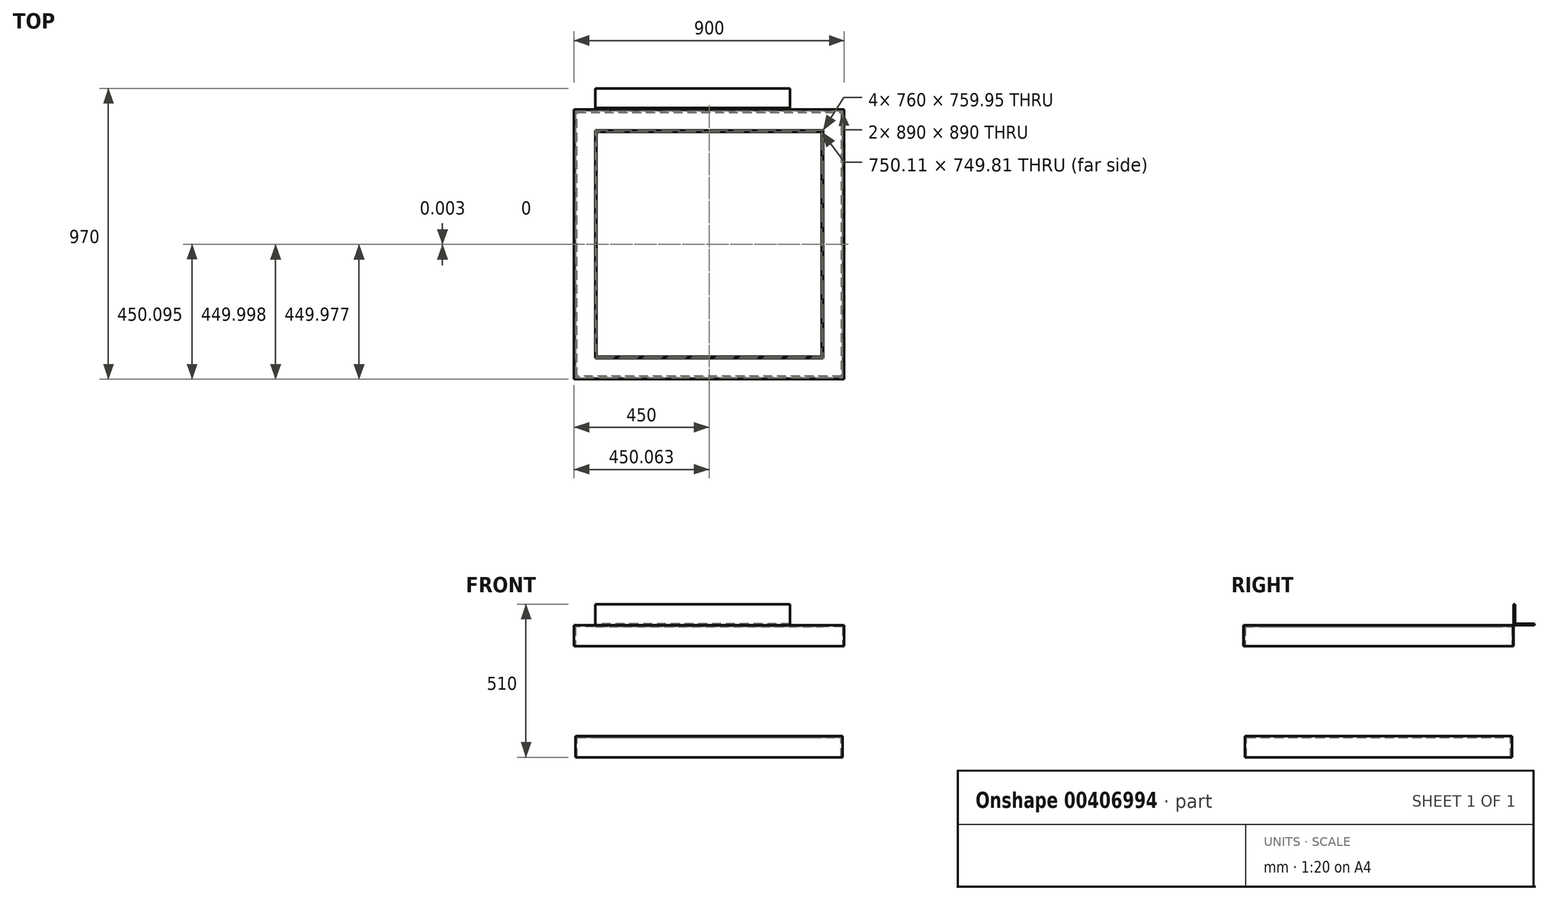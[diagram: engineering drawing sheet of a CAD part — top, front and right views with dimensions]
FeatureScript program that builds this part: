
annotation { "Feature Type Name" : "Feature", "Feature Type Description" : "" }
export const myFeature = defineFeature(function(context is Context, id is Id, definition is map)
    precondition{}
    {
        {
            var Q0;
            Q0=qCreatedBy(makeId("Top.planeOp"),FACE);
            var sketch = newSketch(context, id + "F0", { "sketchPlane" : qUnion([Q0])});
            skLineSegment(sketch, "E0", {"start": v(0, 0) * mm, "end": v(0, -900) * mm});
            skLineSegment(sketch, "E1", {"start": v(0, 0) * mm, "end": v(900, 0) * mm});
            skLineSegment(sketch, "E2", {"start": v(900, 0) * mm, "end": v(900, -899.42) * mm});
            skLineSegment(sketch, "E3", {"start": v(900, -899.42) * mm, "end": v(0, -900) * mm});
            skSolve(sketch);
        }
        {
            var Q0;
            Q0=qCreatedBy(makeId("Front.planeOp"),FACE);
            cPlane(context, id + "F1", {"entities" : qUnion([Q0]), "cplaneType" : CPlaneType.OFFSET, "offset" : 450 * mm, "width" : 150 * mm, "height" : 150 * mm});
        }
        {
            var Q0;
            Q0=qCreatedBy(id+"F1.planeOp",FACE);
            var sketch = newSketch(context, id + "F2", { "sketchPlane" : qUnion([Q0])});
            skLineSegment(sketch, "E4", {"start": v(0, 0) * mm, "end": v(70, 0) * mm});
            skLineSegment(sketch, "E5", {"start": v(70, 0) * mm, "end": v(70, -5) * mm});
            skLineSegment(sketch, "E6", {"start": v(0, -70) * mm, "end": v(0, 0) * mm});
            skLineSegment(sketch, "E7", {"start": v(70, -5) * mm, "end": v(5, -5) * mm});
            skLineSegment(sketch, "E8", {"start": v(5, -5) * mm, "end": v(5, -70) * mm});
            skLineSegment(sketch, "E9", {"start": v(5, -70) * mm, "end": v(0, -70) * mm});
            skSolve(sketch);
        }
        {
            var Q0;
            Q0 = qSketchRegion(id + "F2", true);
            var Q1;
            Q1 = qConstructionFilter(qBodyType(qCreatedBy(id + "F0" ,EDGE), BodyType.WIRE), ConstructionObject.NO);
            sweep(context, id + "F3", {"profiles" : qUnion([Q0]), "path" : qUnion([Q1])});
        }
        {
            var Q0;
            Q0=makeQuery(id+"F3.opSweep","SWEPT_FACE",FACE,{"disambiguationData":[OSD([sQuery(id+"F0.wireOp",EDGE,"E0"),sQuery(id+"F2.wireOp",EDGE,"E9")])]});
            var sketch = newSketch(context, id + "F4", { "sketchPlane" : qUnion([Q0])});
            skLineSegment(sketch, "E10", {"start": v(0, 0) * mm, "end": v(0, 70) * mm});
            skLineSegment(sketch, "E11", {"start": v(0, 70) * mm, "end": v(5, 70) * mm});
            skLineSegment(sketch, "E12", {"start": v(5, 70) * mm, "end": v(5, 5) * mm});
            skLineSegment(sketch, "E13", {"start": v(5, 5) * mm, "end": v(70, 5) * mm});
            skLineSegment(sketch, "E14", {"start": v(70, 5) * mm, "end": v(70, 0) * mm});
            skLineSegment(sketch, "E15", {"start": v(70, 0) * mm, "end": v(0, 0) * mm});
            skSolve(sketch);
        }
        {
            var Q0;
            Q0 = qSketchRegion(id + "F4", true);
            extrude(context, id + "F5", {"entities" : qUnion([Q0]), "operationType" : NewBodyOperationType.ADD, "depth" : 650 * mm});
        }
        {
            var Q0;
            Q0=makeQuery(id+"F3.opSweep","SWEPT_BODY",BODY,{"disambiguationData":[OSD([sQuery(id+"F0.wireOp",EDGE,"E1"),sQuery(id+"F2.wireOp",EDGE,"E4"),sQuery(id+"F2.wireOp",EDGE,"E5"),sQuery(id+"F2.wireOp",EDGE,"E6"),sQuery(id+"F2.wireOp",EDGE,"E7"),sQuery(id+"F2.wireOp",EDGE,"E8"),sQuery(id+"F2.wireOp",EDGE,"E9")])]});
            var Q1;
            Q1=qCreatedBy(id+"F1.planeOp",FACE);
            mirror(context, id + "F6", {"entities" : qUnion([Q0]), "mirrorPlane" : qUnion([Q1])});
        }
        {
            var Q0;
            Q0=qCreatedBy(makeId("Right.planeOp"),FACE);
            cPlane(context, id + "F7", {"entities" : qUnion([Q0]), "cplaneType" : CPlaneType.OFFSET, "offset" : 450 * mm, "width" : 150 * mm, "height" : 150 * mm});
        }
        {
            var Q0;
            Q0=makeQuery(id+"F6.opPattern","COPY",BODY,{"derivedFrom":makeQuery(id+"F3.opSweep","SWEPT_BODY",BODY,{"disambiguationData":[OSD([sQuery(id+"F0.wireOp",EDGE,"E1"),sQuery(id+"F2.wireOp",EDGE,"E4"),sQuery(id+"F2.wireOp",EDGE,"E5"),sQuery(id+"F2.wireOp",EDGE,"E6"),sQuery(id+"F2.wireOp",EDGE,"E7"),sQuery(id+"F2.wireOp",EDGE,"E8"),sQuery(id+"F2.wireOp",EDGE,"E9")])]}),"instanceName":"1"});
            var Q1;
            Q1=makeQuery(id+"F3.opSweep","SWEPT_BODY",BODY,{"disambiguationData":[OSD([sQuery(id+"F0.wireOp",EDGE,"E1"),sQuery(id+"F2.wireOp",EDGE,"E4"),sQuery(id+"F2.wireOp",EDGE,"E5"),sQuery(id+"F2.wireOp",EDGE,"E6"),sQuery(id+"F2.wireOp",EDGE,"E7"),sQuery(id+"F2.wireOp",EDGE,"E8"),sQuery(id+"F2.wireOp",EDGE,"E9")])]});
            var Q2;
            Q2=qCreatedBy(id+"F7.planeOp",FACE);
            mirror(context, id + "F8", {"entities" : qUnion([Q0, Q1]), "mirrorPlane" : qUnion([Q2])});
        }
        {
            var Q0;
            Q0=qCreatedBy(id+"F7.planeOp",FACE);
            var sketch = newSketch(context, id + "F9", { "sketchPlane" : qUnion([Q0])});
            skLineSegment(sketch, "E16", {"start": v(-70, -128.07) * mm, "end": v(-70, -133.07) * mm});
            skLineSegment(sketch, "E17", {"start": v(-5, -370) * mm, "end": v(-5, -440) * mm});
            skLineSegment(sketch, "E18", {"start": v(-5, -370) * mm, "end": v(-75, -370) * mm});
            skLineSegment(sketch, "E19", {"start": v(-75, -370) * mm, "end": v(-75, -375) * mm});
            skLineSegment(sketch, "E20", {"start": v(-75, -375) * mm, "end": v(-10, -375) * mm});
            skLineSegment(sketch, "E21", {"start": v(-10, -375) * mm, "end": v(-10, -440) * mm});
            skLineSegment(sketch, "E22", {"start": v(-10, -440) * mm, "end": v(-5, -440) * mm});
            skSolve(sketch);
        }
        {
            var Q0;
            Q0=qCreatedBy(makeId("Top.planeOp"),FACE);
            var Q1;
            Q1=sQuery(id+"F9.wireOp",VERTEX,"E18.start");
            cPlane(context, id + "F10", {"entities" : qUnion([Q0, Q1]), "cplaneType" : CPlaneType.PLANE_POINT, "offset" : 25 * mm, "oppositeDirection" : true, "width" : 150 * mm, "height" : 150 * mm});
        }
        {
            var Q0;
            Q0=qCreatedBy(id+"F10.planeOp",FACE);
            var sketch = newSketch(context, id + "F11", { "sketchPlane" : qUnion([Q0])});
            skLineSegment(sketch, "E23", {"start": v(450.09, -5.1) * mm, "end": v(894.99, -5.1) * mm});
            skLineSegment(sketch, "E24", {"start": v(450.09, -5.1) * mm, "end": v(5.11, -5.1) * mm});
            skLineSegment(sketch, "E25", {"start": v(5.11, -5.1) * mm, "end": v(5.11, -894.7) * mm});
            skLineSegment(sketch, "E26", {"start": v(5.11, -894.7) * mm, "end": v(895.01, -894.7) * mm});
            skLineSegment(sketch, "E27", {"start": v(895.01, -894.7) * mm, "end": v(894.99, -5.1) * mm});
            skSolve(sketch);
        }
        {
            var Q0;
            Q0 = qSketchRegion(id + "F9", true);
            var Q1;
            Q1 = qConstructionFilter(qBodyType(qCreatedBy(id + "F11" ,EDGE), BodyType.WIRE), ConstructionObject.NO);
            sweep(context, id + "F12", {"profiles" : qUnion([Q0]), "path" : qUnion([Q1])});
        }
    });
